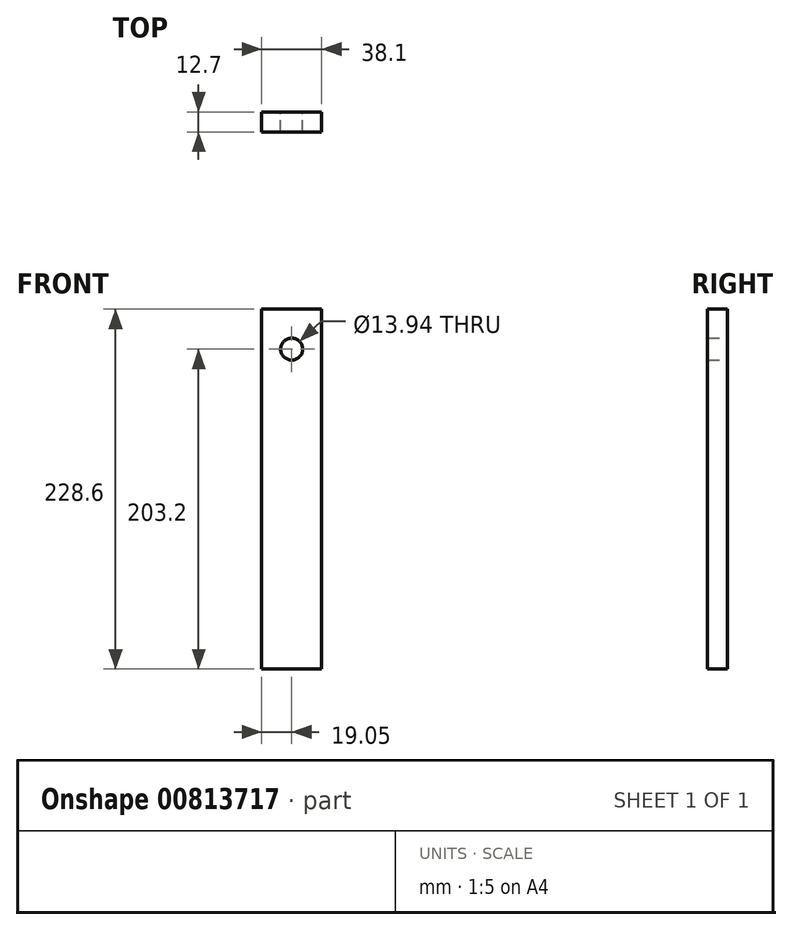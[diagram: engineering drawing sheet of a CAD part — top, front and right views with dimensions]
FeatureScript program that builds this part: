
annotation { "Feature Type Name" : "Feature", "Feature Type Description" : "" }
export const myFeature = defineFeature(function(context is Context, id is Id, definition is map)
    precondition{}
    {
        {
            var Q0;
            Q0=qCreatedBy(makeId("Front.planeOp"),FACE);
            var sketch = newSketch(context, id + "F0", { "sketchPlane" : qUnion([Q0])});
            skLineSegment(sketch, "E0.bottom", {"start": v(-19.05, 114.3) * mm, "end": v(19.05, 114.3) * mm});
            skLineSegment(sketch, "E0.top", {"start": v(-19.05, -114.3) * mm, "end": v(19.05, -114.3) * mm});
            skLineSegment(sketch, "E0.left", {"start": v(-19.05, 114.3) * mm, "end": v(-19.05, -114.3) * mm});
            skLineSegment(sketch, "E0.right", {"start": v(19.05, 114.3) * mm, "end": v(19.05, -114.3) * mm});
            skPoint(sketch, "E0.middle", {"position": v(0, 0) * mm});
            skLineSegment(sketch, "E1", {"start": v(0, 145.78) * mm, "end": v(0, 23.66) * mm, "construction": true});
            skLineSegment(sketch, "E2", {"start": v(-39.1, 88.9) * mm, "end": v(58.35, 88.9) * mm, "construction": true});
            skCircle(sketch, "E3", {"center": v(0, 88.9) * mm, "radius": 6.97 * mm});
            skSolve(sketch);
        }
        {
            var Q0;
            Q0 = qSketchRegion(id + "F0", true);
            extrude(context, id + "F1", {"entities" : qUnion([Q0]), "depth" : 12.7 * mm, "offsetDistance" : 25.4 * mm});
        }
    });
